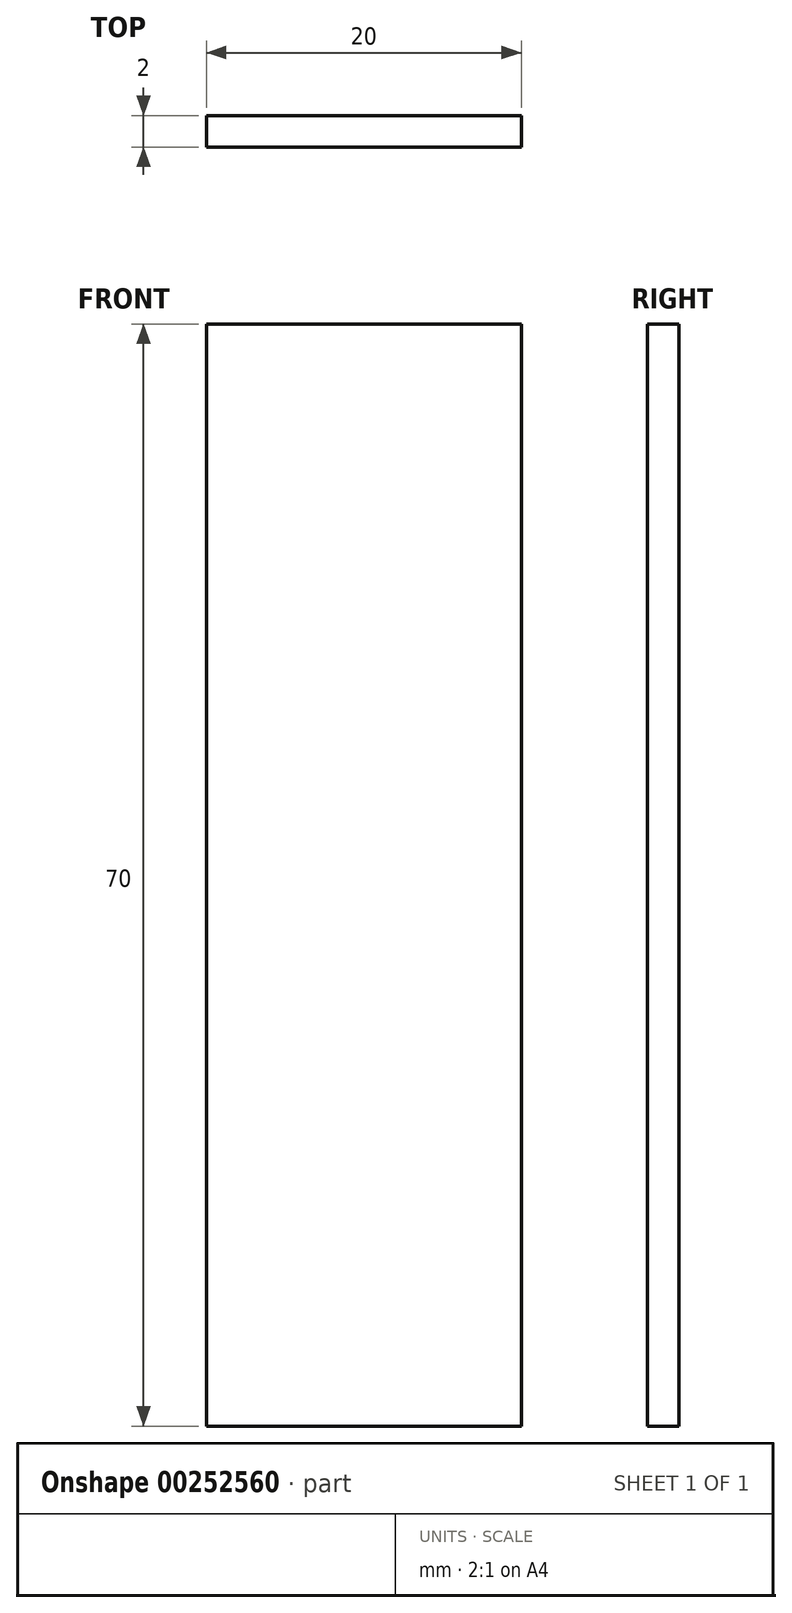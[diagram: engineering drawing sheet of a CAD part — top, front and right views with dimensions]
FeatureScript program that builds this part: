
annotation { "Feature Type Name" : "Feature", "Feature Type Description" : "" }
export const myFeature = defineFeature(function(context is Context, id is Id, definition is map)
    precondition{}
    {
        {
            var Q0;
            Q0=qCreatedBy(makeId("Front.planeOp"),FACE);
            var sketch = newSketch(context, id + "F0", { "sketchPlane" : qUnion([Q0])});
            skLineSegment(sketch, "E0.bottom", {"start": v(10, 35) * mm, "end": v(-10, 35) * mm});
            skLineSegment(sketch, "E0.top", {"start": v(10, -35) * mm, "end": v(-10, -35) * mm});
            skLineSegment(sketch, "E0.left", {"start": v(10, 35) * mm, "end": v(10, -35) * mm});
            skLineSegment(sketch, "E0.right", {"start": v(-10, 35) * mm, "end": v(-10, -35) * mm});
            skPoint(sketch, "E0.middle", {"position": v(0, 0) * mm});
            skSolve(sketch);
        }
        {
            var Q0;
            Q0=makeQuery(id+"F0.imprint","IMPRINT",FACE,{"disambiguationData":[TD([[makeQuery(id+"F0.imprint","IMPRINT",EDGE,{"derivedFrom":sQuery(id+"F0.wireOp",EDGE,"E0.bottom")}),1.0]])]});
            extrude(context, id + "F1", {"entities" : qUnion([Q0]), "depth" : 2 * mm});
        }
    });
